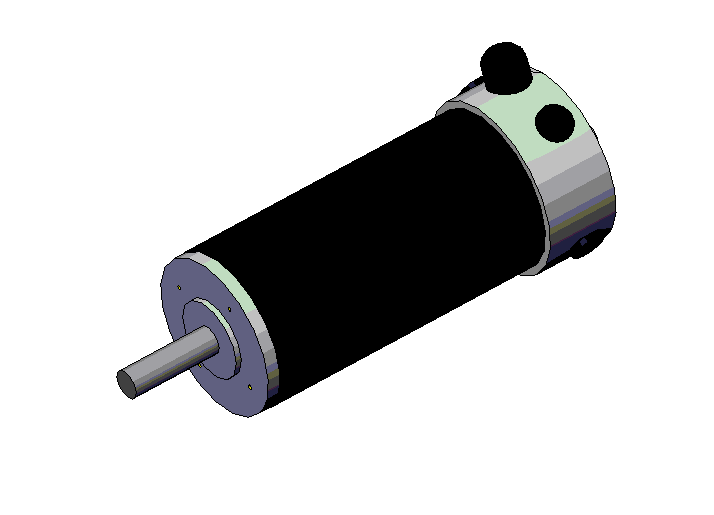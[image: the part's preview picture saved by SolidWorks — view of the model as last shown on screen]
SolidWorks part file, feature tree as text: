
SOLIDWORKS PART (.sldprt)
format: sldprt  version: not decoded by parser v0  size: 277,504 bytes
history: native  units: mm
features: sketch x14, extrude x11, plane x6, fillet x1 (+7 scaffold rows collapsed)
feature tree (39):
  scaffold x7  (default folders/planes/origin — collapsed)
  plane  "Plane1"
  plane  "Plane2"
  plane  "Plane3"
  sketch  "Sketch1"  dims[D1=~4.063954mm]
  extrude  "Base-Extrude"  Depth=165.1mm
  sketch  "Sketch2"  dims[D1=~49.595085mm]
  extrude  "Boss-Extrude1"  Depth=32.766mm
  sketch  "Sketch3"  dims[D1=~8.980256mm]
  extrude  "Boss-Extrude2"  Depth=49.784mm
  sketch  "Sketch4"  dims[D1=~13.73715mm]
  extrude  "Boss-Extrude3"  Depth=8.382mm
  sketch  "Sketch5"
  sketch  "Sketch6"
  plane  "Plane4"
  sketch  "Sketch7"  dims[D1=~9.919017mm]
  extrude  "Boss-Extrude5"  Depth=40.386mm
  sketch  "Sketch9"
  extrude  "Boss-Extrude7"  Depth=80.772mm
  sketch  "Sketch10"
  plane  "Plane5"
  sketch  "Sketch11"  dims[D1=12.5095mm]
  extrude  "Boss-Extrude8"  Depth=40.386mm
  sketch  "Sketch12"  dims[D1=12.5095mm]
  extrude  "Boss-Extrude10"  Depth=80.772mm
  plane  "Plane6"
  sketch  "Sketch13"  dims[D1=36.83mm]
  extrude  "Boss-Extrude11"  Depth=53.975mm
  fillet  "Fillet1"  Radius=6.35mm
  sketch  "Sketch14"  dims[D1=~7.405309mm]
  extrude  "Boss-Extrude12"  Depth=16.002mm
  sketch  "Sketch15"  dims[D1=35.306mm]
  extrude  "Boss-Extrude13"  Depth=5.842mm
decode coverage: 22 of 26 modeling features carry decoded parameters
note: ~ marks probable driven/reference dimensions
note: suppression state not decoded; provenance and decode notes live in map.json
